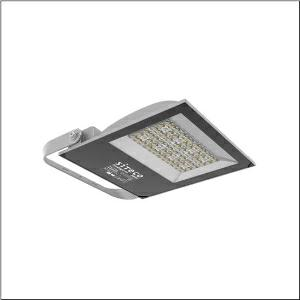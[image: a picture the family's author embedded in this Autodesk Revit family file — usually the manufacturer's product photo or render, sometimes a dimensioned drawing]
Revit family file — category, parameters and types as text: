
# Revit family: floodlight_fl_41_midi___pl32_5xa8581b1121_55a4
name_source: partatom
category: Lighting Fixtures
units: mm (PartAtom-declared; Revit-internal decimal feet)

## family parameters
Cut with Voids When Loaded = No
Host = Face
Light Source = No
Part Type = Normal
Room Calculation Point = No
Round Connector Dimension = Use Diameter
Shared = No

## types (1)
- --- (1 x LED, 26000 lm, 200 W, 3000K)
    Apparent Load = 200 VA
    CIE Flux Codes = 38 75 98 100 100
    Color Rendering = 70
    Color Temperature = 3000K
    Default Elevation = 1800 mm
    Description = Floodlight FL 41 midi, floodlight, primary light control with lens, of PMMA, primary optical cover: protective disc, transparent, light distribution: PL32, light emission: direct distribution, installation type: surface-mounted, LED, High Power LED, rated luminous flux: 26.000lm, luminous efficacy: 130lm/W, light colour: 730, colour temperature: 3000K, control gear: ON/OFF Multilumen, with cable, 3x 1.5mm², mains connection: 220..240V, AC, 50/60Hz, connection cable pre-assembled, cable length: 2m, rated input power: 200W, luminaire housing, of diecast aluminium, powder-coated, metallic grey (RAL 9006), length: 375mm, width: 335mm, height: 65mm, protection rating (complete): IP65, insulation class (complete): insulation class I (protective earthing), certification: CE, ENEC, impact resistance: IK08, permissible operating ambient temperature: -40..+40°C, permissible storage temperature: -40..+60°C, packaging unit: 1 piece

Light Distribution: PL32
    Height = 66 mm
    Lamp = 1 x LED
    Lamp Light Flux = 26000 lm
    Lamp Power = 200 W
    Lamp count = 1
    Length = 323 mm
    Luminous efficacy = 130 lm/W
    Manufacturer = Siteco
    ModVariant = No
    Model = 5XA8581B1121
    Mounting Place = Ceiling
    Mounting Type = Surface mounted
    Number of Poles = 1
    OnlyDefault = Yes
    Power Factor = 1
    Product Name = Floodlight FL 41 midi | PL32
    Product group = floodlight | ceiling mounted
    ProductGroupID = 305
    Protection Class = Protection class I
    Protection Degree = IP 65
    RLX_Detail_Level = 1
    RLX_Emergency_Light_Flux = 0 lm
    RLX_Emergency_Type = 0
    RLX_Emergency_Type_DB = No
    RlxData = <blob elided: 27425 chars, md5=944e938f>
    Socket = socket
    Standby Power = 0 W
    System Light Flux = 26000 lm
    System Power = 200 W
    Type Comments = factory setting: luminous flux: 100 % | (OFF | OFF | OFF)
    Type Image = l_1248229.jpg
    URL = http://relux.com
    VarID = @adj_132757
    Voltage = 0 V
    Weight = 0.00 kg
    Width = 331 mm

## geometry (parser evidence)
native form markers: Blend x4, Sweep x9
no freeform markers — native parametric forms only
